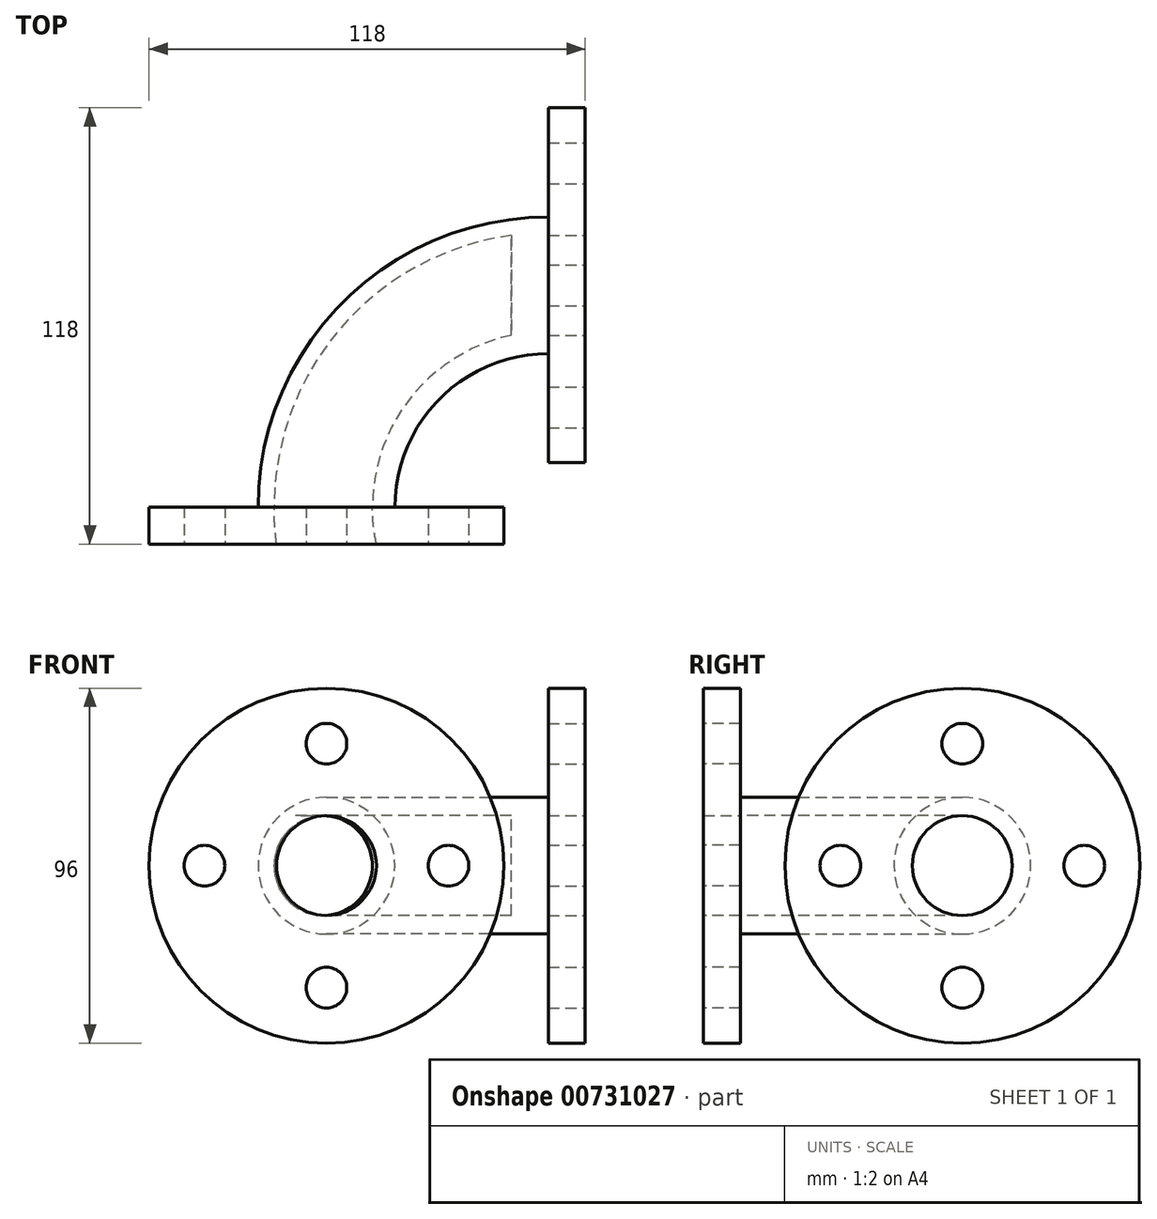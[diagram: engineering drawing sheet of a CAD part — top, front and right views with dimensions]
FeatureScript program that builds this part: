
annotation { "Feature Type Name" : "Feature", "Feature Type Description" : "" }
export const myFeature = defineFeature(function(context is Context, id is Id, definition is map)
    precondition{}
    {
        {
            var Q0;
            Q0=qCreatedBy(makeId("Top.planeOp"),FACE);
            var sketch = newSketch(context, id + "F0", { "sketchPlane" : qUnion([Q0])});
            skArc(sketch, "E0", {"start": v(-60, 0) * mm, "mid": v(-42.43, 42.43) * mm, "end": v(0, 60) * mm});
            skSolve(sketch);
        }
        {
            var Q0;
            Q0=qCreatedBy(makeId("Front.planeOp"),FACE);
            var sketch = newSketch(context, id + "F1", { "sketchPlane" : qUnion([Q0])});
            skCircle(sketch, "E1", {"center": v(-60, 0) * mm, "radius": 48 * mm});
            skSolve(sketch);
        }
        {
            var Q0;
            Q0=qCreatedBy(makeId("Right.planeOp"),FACE);
            var sketch = newSketch(context, id + "F2", { "sketchPlane" : qUnion([Q0])});
            skCircle(sketch, "E2", {"center": v(60, 0) * mm, "radius": 48 * mm});
            skSolve(sketch);
        }
        {
            var Q0;
            Q0=makeQuery(id+"F1.imprint","IMPRINT",FACE,{"disambiguationData":[TD([[makeQuery(id+"F1.imprint","IMPRINT",EDGE,{"derivedFrom":sQuery(id+"F1.wireOp",EDGE,"E1")}),1.0]])]});
            extrude(context, id + "F3", {"entities" : qUnion([Q0]), "depth" : 10 * mm, "offsetDistance" : 25 * mm});
        }
        {
            var Q0;
            Q0=makeQuery(id+"F2.imprint","IMPRINT",FACE,{"disambiguationData":[TD([[makeQuery(id+"F2.imprint","IMPRINT",EDGE,{"derivedFrom":sQuery(id+"F2.wireOp",EDGE,"E2")}),1.0]])]});
            extrude(context, id + "F4", {"entities" : qUnion([Q0]), "depth" : 10 * mm, "offsetDistance" : 25 * mm});
        }
        {
            var Q0;
            Q0=makeQuery(id+"F3.opExtrude","CAP_FACE",FACE,{"disambiguationData":[OSD([sQuery(id+"F1.wireOp",EDGE,"E1")])],"isStart":true});
            var sketch = newSketch(context, id + "F5", { "sketchPlane" : qUnion([Q0])});
            skCircle(sketch, "E3", {"center": v(60, 0) * mm, "radius": 18.5 * mm});
            skSolve(sketch);
        }
        {
            var Q0;
            Q0 = qSketchRegion(id + "F5", true);
            var Q1;
            Q1=sQuery(id+"F0.wireOp",EDGE,"E0");
            sweep(context, id + "F6", {"profiles" : qUnion([Q0]), "path" : qUnion([Q1])});
        }
        {
            var Q0;
            Q0=makeQuery(id+"F3.opExtrude","CAP_FACE",FACE,{"disambiguationData":[OSD([sQuery(id+"F1.wireOp",EDGE,"E1")])],"isStart":false});
            var sketch = newSketch(context, id + "F7", { "sketchPlane" : qUnion([Q0])});
            skCircle(sketch, "E4", {"center": v(-60, 0) * mm, "radius": 13.5 * mm});
            skSolve(sketch);
        }
        {
            var Q0;
            Q0 = qSketchRegion(id + "F7", true);
            var Q1;
            Q1=sQuery(id+"F0.wireOp",EDGE,"E0");
            sweep(context, id + "F8", {"operationType" : NewBodyOperationType.REMOVE, "profiles" : qUnion([Q0]), "path" : qUnion([Q1])});
        }
        {
            var Q0;
            Q0=makeQuery(id+"F4.opExtrude","CAP_FACE",FACE,{"disambiguationData":[OSD([sQuery(id+"F2.wireOp",EDGE,"E2")])],"isStart":false});
            var sketch = newSketch(context, id + "F9", { "sketchPlane" : qUnion([Q0])});
            skCircle(sketch, "E5", {"center": v(60, 0) * mm, "radius": 13.5 * mm});
            skSolve(sketch);
        }
        {
            var Q0;
            Q0 = qSketchRegion(id + "F9", true);
            extrude(context, id + "F10", {"entities" : qUnion([Q0]), "operationType" : NewBodyOperationType.REMOVE, "oppositeDirection" : true, "depth" : 10 * mm, "offsetDistance" : 25 * mm});
        }
        {
            var Q0;
            Q0=makeQuery(id+"F3.opExtrude","CAP_FACE",FACE,{"disambiguationData":[OSD([sQuery(id+"F1.wireOp",EDGE,"E1")])],"isStart":false});
            var sketch = newSketch(context, id + "F11", { "sketchPlane" : qUnion([Q0])});
            skCircle(sketch, "E6", {"center": v(-60, 0) * mm, "radius": 33 * mm, "construction": true});
            skCircle(sketch, "E7", {"center": v(-60, 33) * mm, "radius": 5.5 * mm});
            skCircle(sketch, "E8", {"center": v(-27, 0) * mm, "radius": 5.5 * mm});
            skCircle(sketch, "E9", {"center": v(-60, -33) * mm, "radius": 5.5 * mm});
            skCircle(sketch, "E10", {"center": v(-93, 0) * mm, "radius": 5.5 * mm});
            skSolve(sketch);
        }
        {
            var Q0;
            Q0 = qSketchRegion(id + "F11", true);
            extrude(context, id + "F12", {"entities" : qUnion([Q0]), "operationType" : NewBodyOperationType.REMOVE, "oppositeDirection" : true, "depth" : 10 * mm, "offsetDistance" : 25 * mm});
        }
        {
            var Q0;
            Q0=makeQuery(id+"F4.opExtrude","CAP_FACE",FACE,{"disambiguationData":[OSD([sQuery(id+"F2.wireOp",EDGE,"E2")])],"isStart":false});
            var sketch = newSketch(context, id + "F13", { "sketchPlane" : qUnion([Q0])});
            skCircle(sketch, "E11", {"center": v(60, 0) * mm, "radius": 33 * mm, "construction": true});
            skCircle(sketch, "E12", {"center": v(60, 33) * mm, "radius": 5.5 * mm});
            skCircle(sketch, "E13", {"center": v(93, 0) * mm, "radius": 5.5 * mm});
            skCircle(sketch, "E14", {"center": v(60, -33) * mm, "radius": 5.5 * mm});
            skCircle(sketch, "E15", {"center": v(27, 0) * mm, "radius": 5.5 * mm});
            skSolve(sketch);
        }
        {
            var Q0;
            Q0 = qSketchRegion(id + "F13", true);
            extrude(context, id + "F14", {"entities" : qUnion([Q0]), "operationType" : NewBodyOperationType.REMOVE, "oppositeDirection" : true, "depth" : 10 * mm, "offsetDistance" : 25 * mm});
        }
    });
